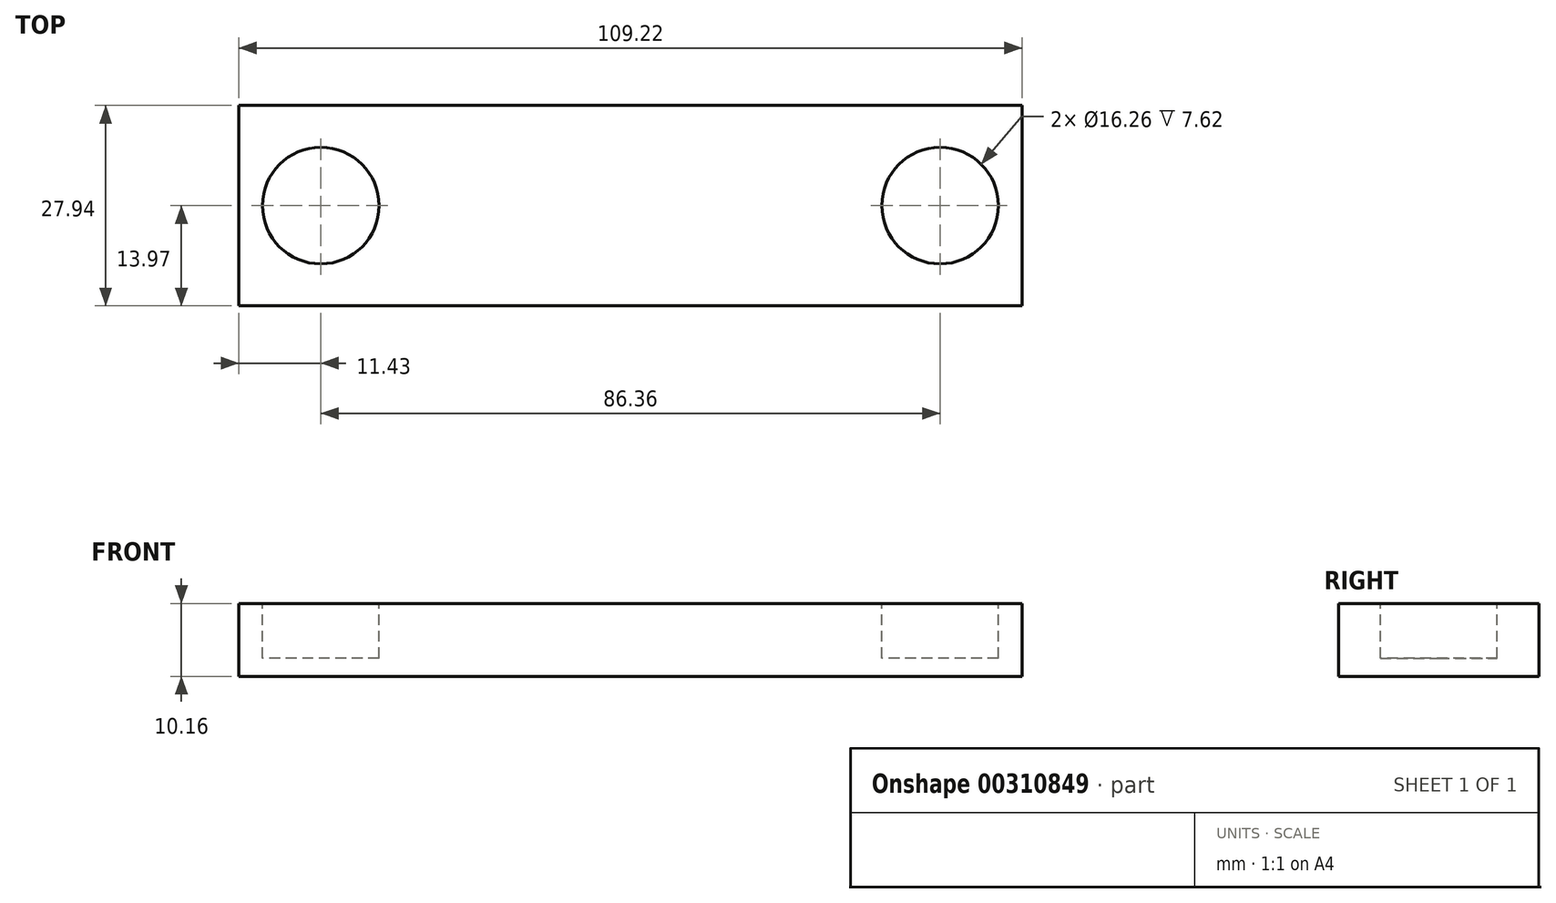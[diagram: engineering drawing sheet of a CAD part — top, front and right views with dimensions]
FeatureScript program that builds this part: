
annotation { "Feature Type Name" : "Feature", "Feature Type Description" : "" }
export const myFeature = defineFeature(function(context is Context, id is Id, definition is map)
    precondition{}
    {
        {
            var Q0;
            Q0=qCreatedBy(makeId("Top.planeOp"),FACE);
            var sketch = newSketch(context, id + "F0", { "sketchPlane" : qUnion([Q0])});
            skLineSegment(sketch, "E0.bottom", {"start": v(54.61, 13.97) * mm, "end": v(-54.61, 13.97) * mm});
            skLineSegment(sketch, "E0.top", {"start": v(54.61, -13.97) * mm, "end": v(-54.61, -13.97) * mm});
            skLineSegment(sketch, "E0.left", {"start": v(54.61, 13.97) * mm, "end": v(54.61, -13.97) * mm});
            skLineSegment(sketch, "E0.right", {"start": v(-54.61, 13.97) * mm, "end": v(-54.61, -13.97) * mm});
            skPoint(sketch, "E0.middle", {"position": v(0, 0) * mm});
            skSolve(sketch);
        }
        {
            var Q0;
            Q0 = qSketchRegion(id + "F0", true);
            extrude(context, id + "F1", {"entities" : qUnion([Q0]), "depth" : 10.16 * mm});
        }
        {
            var Q0;
            Q0=makeQuery(id+"F1.opExtrude","CAP_FACE",FACE,{"disambiguationData":[OSD([sQuery(id+"F0.wireOp",EDGE,"E0.bottom"),sQuery(id+"F0.wireOp",EDGE,"E0.top"),sQuery(id+"F0.wireOp",EDGE,"E0.left"),sQuery(id+"F0.wireOp",EDGE,"E0.right")])],"isStart":false});
            var sketch = newSketch(context, id + "F2", { "sketchPlane" : qUnion([Q0])});
            skCircle(sketch, "E1", {"center": v(-43.18, 0) * mm, "radius": 8.13 * mm});
            skLineSegment(sketch, "E2", {"start": v(0, 0) * mm, "end": v(0, -85.17) * mm, "construction": true});
            skCircle(sketch, "E3.MirrorC", {"center": v(43.18, 0) * mm, "radius": 8.13 * mm});
            skSolve(sketch);
        }
        {
            var Q0;
            Q0 = qSketchRegion(id + "F2", true);
            extrude(context, id + "F3", {"entities" : qUnion([Q0]), "operationType" : NewBodyOperationType.REMOVE, "oppositeDirection" : true, "depth" : 7.62 * mm});
        }
    });
